# Revit family: Focus LCD
name_source: partatom
category: Mechanical Equipment
revit_build: Autodesk Revit 2018 (Build: 20170223_1515(x64)
units: mm (PartAtom-declared; Revit-internal decimal feet)

## family parameters
Always vertical = Yes
Classification = None
Cut with Voids When Loaded = No
OmniClass Number = 23.75.50.11.14.11
OmniClass Title = Boiler Feedwater Pumps
Part Type = Normal
Room Calculation Point = No
Round Connector Dimension = Use Diameter
Shared = No
Work Plane-Based = No

## types (1)
- Focus LCD
    Art. No. = 200 550 027
    Breedte = 245 mm  [stored 0.803806 ft]
    Diepte = 126 mm  [stored 0.413386 ft]
    Hoogte = 440 mm  [stored 1.44357 ft]
    Kunststof grijs mat = Kunststof grijs mat
    Kunststof wit = Kunststof wit
    Manufacturer = Masterwatt B.V.
    Metaal = Metal
    Model = Focus LCD Electronic 27
    Phase = 3
    Power (default) = 27000 VA
    Scherm = Scherm
    Test = Test
    URL = https://masterwatt.nl
    Voltage = 400 V
    Zilver = zilver mat
    Zwart = Zwart

note: [stored X ft] marks values corroborated as IEEE doubles in the binary element streams (Revit-internal decimal feet)

## geometry (parser evidence)
native form markers: Sweep x5
no freeform markers — native parametric forms only
